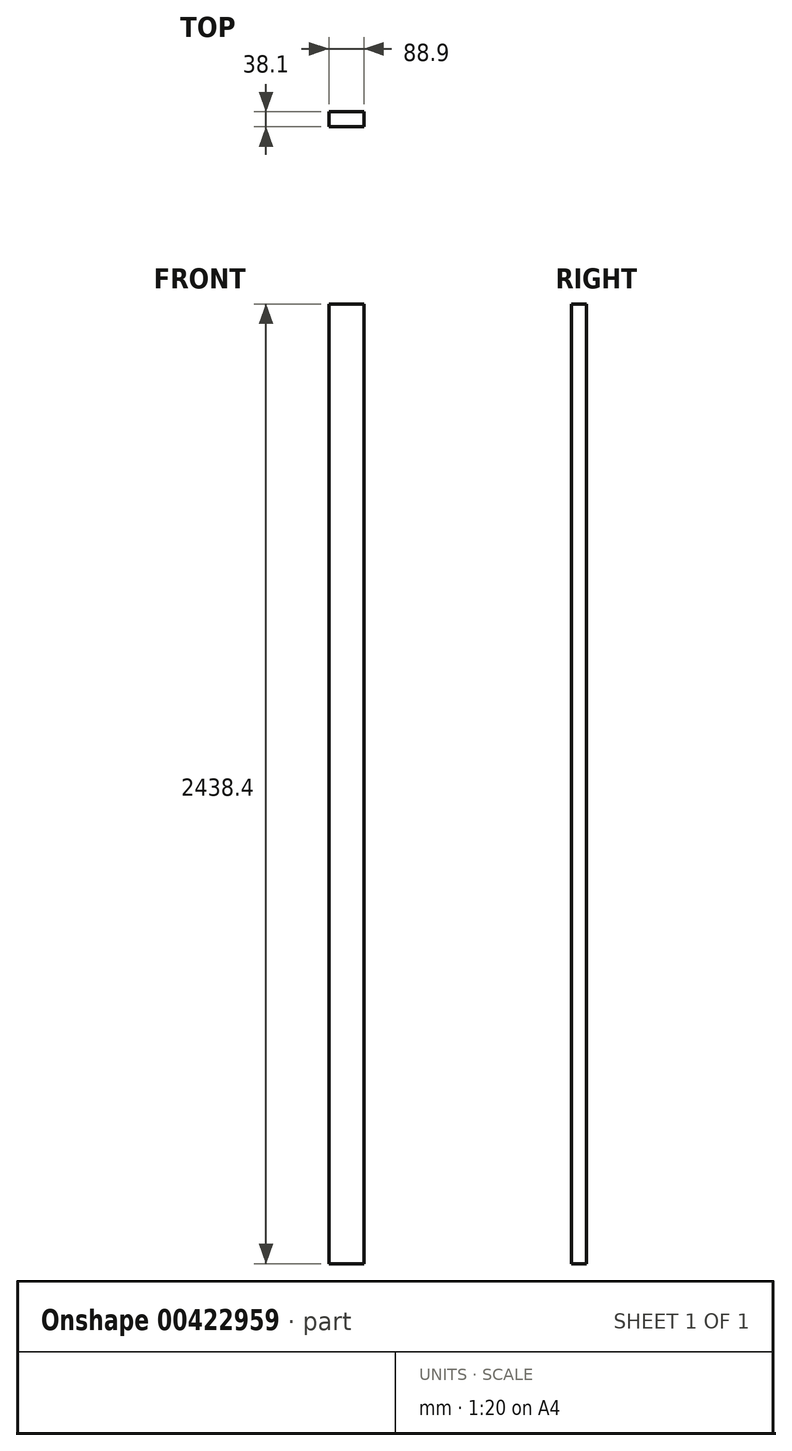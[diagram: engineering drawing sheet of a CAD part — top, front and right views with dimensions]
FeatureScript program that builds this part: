
annotation { "Feature Type Name" : "Feature", "Feature Type Description" : "" }
export const myFeature = defineFeature(function(context is Context, id is Id, definition is map)
    precondition{}
    {
        {
            var Q0;
            Q0=qCreatedBy(makeId("Top.planeOp"),FACE);
            var sketch = newSketch(context, id + "F0", { "sketchPlane" : qUnion([Q0])});
            skLineSegment(sketch, "E0.bottom", {"start": v(44.45, 19.05) * mm, "end": v(-44.45, 19.05) * mm});
            skLineSegment(sketch, "E0.top", {"start": v(44.45, -19.05) * mm, "end": v(-44.45, -19.05) * mm});
            skLineSegment(sketch, "E0.left", {"start": v(44.45, 19.05) * mm, "end": v(44.45, -19.05) * mm});
            skLineSegment(sketch, "E0.right", {"start": v(-44.45, 19.05) * mm, "end": v(-44.45, -19.05) * mm});
            skPoint(sketch, "E0.middle", {"position": v(0, 0) * mm});
            skSolve(sketch);
        }
        {
            var Q0;
            Q0 = qSketchRegion(id + "F0", true);
            extrude(context, id + "F1", {"entities" : qUnion([Q0]), "depth" : 2438.4 * mm, "offsetDistance" : 25.4 * mm});
        }
    });
